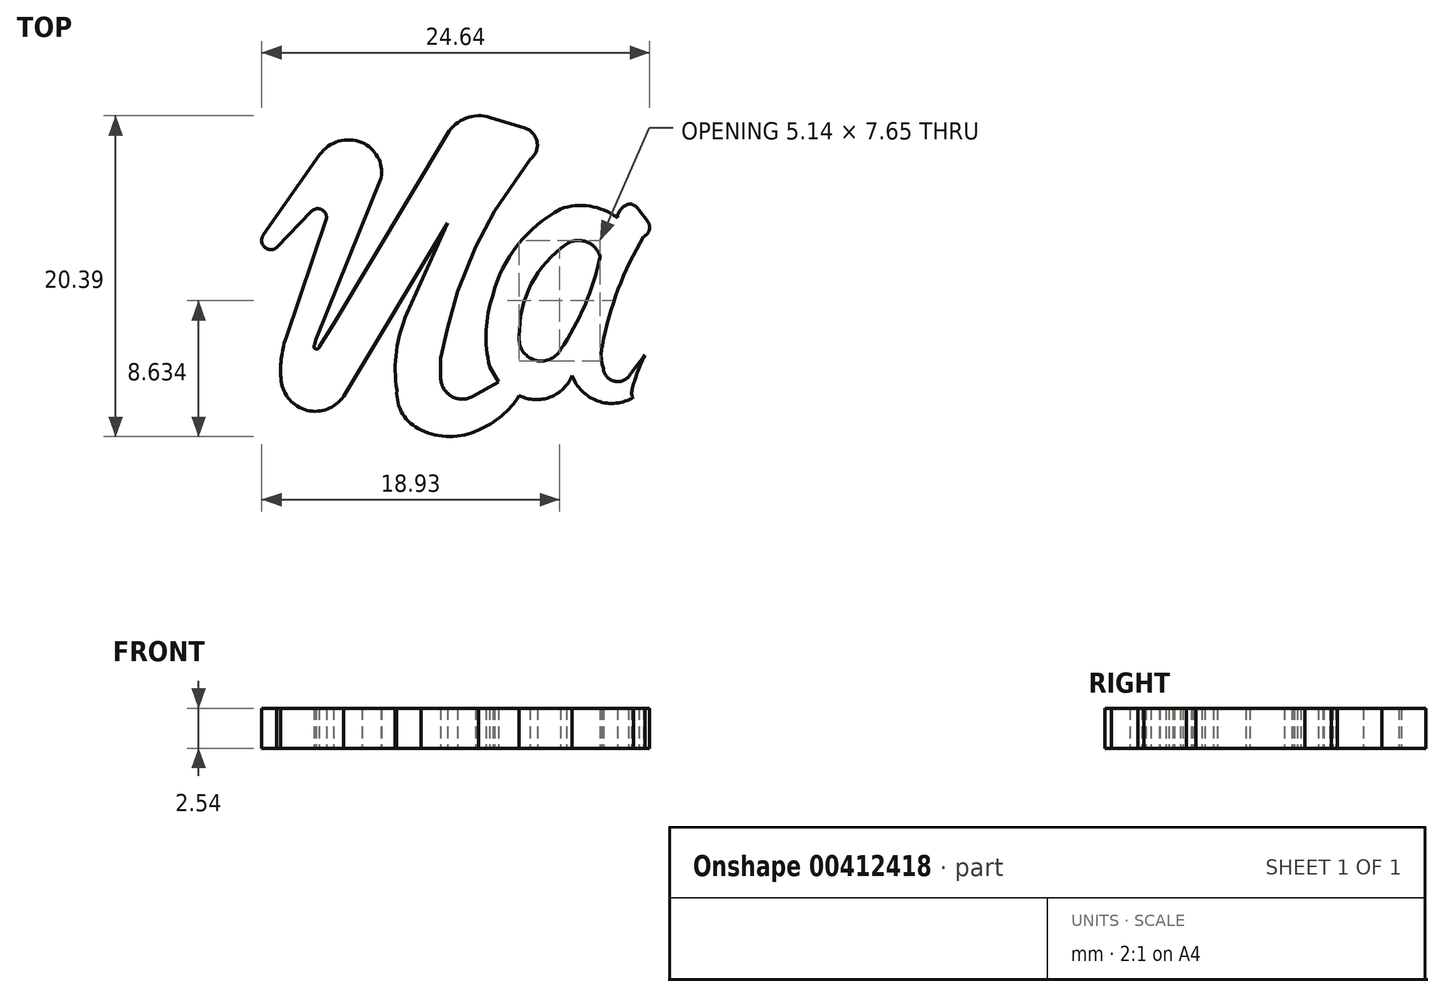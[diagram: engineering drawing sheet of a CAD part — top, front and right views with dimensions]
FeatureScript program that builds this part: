
annotation { "Feature Type Name" : "Feature", "Feature Type Description" : "" }
export const myFeature = defineFeature(function(context is Context, id is Id, definition is map)
    precondition{}
    {
        {
            var Q0;
            Q0=qCreatedBy(makeId("Top.planeOp"),FACE);
            var sketch = newSketch(context, id + "F0", { "sketchPlane" : qUnion([Q0])});
            skArc(sketch, "E0", {"start": v(0.44, -13.61) * mm, "mid": v(0.52, -14.38) * mm, "end": v(1.29, -14.39) * mm});
            skLineSegment(sketch, "E1", {"start": v(0.44, -13.61) * mm, "end": v(4.02, -8.5) * mm});
            skLineSegment(sketch, "E2", {"start": v(1.29, -14.39) * mm, "end": v(3.51, -12.1) * mm});
            skArc(sketch, "E3", {"start": v(6.7, -7.72) * mm, "mid": v(5.22, -7.65) * mm, "end": v(4.02, -8.5) * mm});
            skArc(sketch, "E4", {"start": v(7.92, -9.98) * mm, "mid": v(7.7, -8.64) * mm, "end": v(6.7, -7.72) * mm});
            skLineSegment(sketch, "E5", {"start": v(7.92, -9.98) * mm, "end": v(3.78, -20.22) * mm});
            skLineSegment(sketch, "E6", {"start": v(3.78, -20.22) * mm, "end": v(3.68, -20.57) * mm});
            skLineSegment(sketch, "E7", {"start": v(3.98, -20.73) * mm, "end": v(4.9, -19.24) * mm});
            skArc(sketch, "E8", {"start": v(3.68, -20.57) * mm, "mid": v(3.74, -20.83) * mm, "end": v(3.98, -20.73) * mm});
            skLineSegment(sketch, "E9", {"start": v(4.9, -19.24) * mm, "end": v(12.13, -7.17) * mm});
            skArc(sketch, "E10", {"start": v(14.84, -6.13) * mm, "mid": v(13.3, -6.18) * mm, "end": v(12.13, -7.17) * mm});
            skLineSegment(sketch, "E11", {"start": v(14.84, -6.13) * mm, "end": v(17.05, -6.8) * mm});
            skArc(sketch, "E12", {"start": v(17.36, -8.8) * mm, "mid": v(17.83, -7.7) * mm, "end": v(17.05, -6.8) * mm});
            skLineSegment(sketch, "E13", {"start": v(17.36, -8.8) * mm, "end": v(15.1, -12.1) * mm});
            skLineSegment(sketch, "E14", {"start": v(15.1, -12.1) * mm, "end": v(13.92, -14.37) * mm});
            skLineSegment(sketch, "E15", {"start": v(13.92, -14.37) * mm, "end": v(12.79, -17.18) * mm});
            skLineSegment(sketch, "E16", {"start": v(12.79, -17.18) * mm, "end": v(12.15, -19.5) * mm});
            skLineSegment(sketch, "E17", {"start": v(12.15, -19.5) * mm, "end": v(11.7, -21.43) * mm});
            skLineSegment(sketch, "E18", {"start": v(11.7, -21.43) * mm, "end": v(11.7, -22.67) * mm});
            skArc(sketch, "E19", {"start": v(11.7, -22.67) * mm, "mid": v(12.37, -23.84) * mm, "end": v(13.73, -23.85) * mm});
            skLineSegment(sketch, "E20", {"start": v(13.73, -23.85) * mm, "end": v(15.36, -22.93) * mm});
            skLineSegment(sketch, "E21", {"start": v(15.36, -22.93) * mm, "end": v(14.82, -21.97) * mm});
            skArc(sketch, "E22", {"start": v(15.01, -17.43) * mm, "mid": v(14.59, -19.68) * mm, "end": v(14.82, -21.97) * mm});
            skArc(sketch, "E23", {"start": v(19.3, -11.94) * mm, "mid": v(16.6, -14.24) * mm, "end": v(15.01, -17.43) * mm});
            skArc(sketch, "E24", {"start": v(22.92, -12.49) * mm, "mid": v(21.18, -11.77) * mm, "end": v(19.3, -11.94) * mm});
            skArc(sketch, "E25", {"start": v(21.83, -15) * mm, "mid": v(20.98, -14.04) * mm, "end": v(19.7, -14.17) * mm});
            skArc(sketch, "E26", {"start": v(16.7, -20.05) * mm, "mid": v(17.66, -21.54) * mm, "end": v(19.3, -20.89) * mm});
            skArc(sketch, "E27", {"start": v(19.7, -14.17) * mm, "mid": v(17.45, -16.73) * mm, "end": v(16.7, -20.05) * mm});
            skArc(sketch, "E28", {"start": v(19.3, -20.89) * mm, "mid": v(20.86, -18.07) * mm, "end": v(21.83, -15) * mm});
            skArc(sketch, "E29", {"start": v(16.7, -23.8) * mm, "mid": v(18.65, -23.9) * mm, "end": v(20.05, -22.52) * mm});
            skArc(sketch, "E30", {"start": v(22.03, -22.07) * mm, "mid": v(22.82, -22.9) * mm, "end": v(23.8, -22.32) * mm});
            skArc(sketch, "E31", {"start": v(20.05, -22.52) * mm, "mid": v(21.67, -24.14) * mm, "end": v(23.95, -23.9) * mm});
            skArc(sketch, "E32", {"start": v(1.57, -22.86) * mm, "mid": v(3.2, -24.73) * mm, "end": v(5.52, -23.85) * mm});
            skArc(sketch, "E33", {"start": v(4.44, -12.54) * mm, "mid": v(4.13, -11.98) * mm, "end": v(3.51, -12.1) * mm});
            skLineSegment(sketch, "E34", {"start": v(4.44, -12.54) * mm, "end": v(1.87, -20.15) * mm});
            skArc(sketch, "E35", {"start": v(1.87, -20.15) * mm, "mid": v(1.57, -21.49) * mm, "end": v(1.57, -22.86) * mm});
            skLineSegment(sketch, "E36", {"start": v(5.52, -23.85) * mm, "end": v(12.15, -12.83) * mm});
            skLineSegment(sketch, "E37", {"start": v(12.15, -12.83) * mm, "end": v(9.58, -18.57) * mm});
            skArc(sketch, "E38", {"start": v(9.58, -18.57) * mm, "mid": v(8.9, -20.97) * mm, "end": v(8.92, -23.46) * mm});
            skArc(sketch, "E39", {"start": v(8.92, -23.46) * mm, "mid": v(9.29, -24.97) * mm, "end": v(10.45, -25.98) * mm});
            skArc(sketch, "E40", {"start": v(10.45, -25.98) * mm, "mid": v(12.28, -26.4) * mm, "end": v(14.1, -25.98) * mm});
            skArc(sketch, "E41", {"start": v(14.1, -25.98) * mm, "mid": v(15.57, -25.1) * mm, "end": v(16.7, -23.8) * mm});
            skArc(sketch, "E42", {"start": v(23.64, -11.63) * mm, "mid": v(23.16, -11.95) * mm, "end": v(22.92, -12.49) * mm});
            skArc(sketch, "E43", {"start": v(24.29, -12.02) * mm, "mid": v(24.02, -11.73) * mm, "end": v(23.64, -11.63) * mm});
            skLineSegment(sketch, "E44", {"start": v(24.29, -12.02) * mm, "end": v(24.83, -12.71) * mm});
            skArc(sketch, "E45", {"start": v(24.58, -13.7) * mm, "mid": v(24.95, -13.27) * mm, "end": v(24.83, -12.71) * mm});
            skArc(sketch, "E46", {"start": v(24.58, -13.7) * mm, "mid": v(22.97, -17.05) * mm, "end": v(21.96, -20.62) * mm});
            skArc(sketch, "E47", {"start": v(21.96, -20.62) * mm, "mid": v(21.9, -21.35) * mm, "end": v(22.03, -22.07) * mm});
            skFitSpline(sketch, "E48", {"points": [v(24.66, -21.23) * mm, v(26.09, -18.34) * mm, v(26.73, -14.68) * mm, v(26.2, -10.48) * mm, v(25.33, -8.21) * mm, v(25.34, -7.66) * mm, v(25.92, -7.22) * mm, v(27.77, -6.23) * mm, v(28.48, -6.17) * mm, v(28.83, -6.67) * mm, v(29.15, -9.2) * mm, v(29.21, -11.8) * mm, v(29.15, -14.25) * mm, v(29.13, -15.57) * mm, v(29.38, -15.18) * mm, v(29.75, -13.94) * mm, v(31.5, -7) * mm, v(31.92, -5.4) * mm, v(32.5, -4.97) * mm, v(33.79, -4.6) * mm, v(36.42, -4.48) * mm, v(36.99, -4.63) * mm, v(37.3, -5.31) * mm, v(37.06, -6.27) * mm, v(34.06, -14.63) * mm, v(33.67, -15.91) * mm, v(33.91, -15.61) * mm, v(35.35, -12.6) * mm, v(37.8, -7.41) * mm, v(38.27, -6.47) * mm, v(38.71, -5.86) * mm, v(39.24, -5.62) * mm, v(40.15, -5.89) * mm, v(41.89, -7.18) * mm, v(42.06, -7.68) * mm, v(41.74, -8.68) * mm, v(40.21, -11.59) * mm, v(39.27, -14.16) * mm, v(38.3, -17.42) * mm, v(38.44, -19.03) * mm, v(38.82, -20.12) * mm, v(39.65, -20.71) * mm, v(39.7, -20.21) * mm, v(39.76, -18.01) * mm, v(41.06, -14.98) * mm, v(42.18, -13.3) * mm, v(43.17, -12.26) * mm, v(44.34, -11.64) * mm, v(45.3, -11.45) * mm, v(46.51, -11.49) * mm, v(47.7, -11.9) * mm, v(47.96, -12.1) * mm, v(48.46, -11.3) * mm, v(48.95, -11.15) * mm, v(50.1, -12.6) * mm, v(49.94, -13.05) * mm, v(48.65, -15.34) * mm, v(47.36, -18.98) * mm, v(47.1, -20.7) * mm, v(47.16, -21.54) * mm, v(47.61, -22.32) * mm, v(48.25, -22.7) * mm, v(50.37, -19.94) * mm, v(50.56, -17.82) * mm, v(50.69, -15) * mm, v(51.26, -13.7) * mm, v(52.16, -12.95) * mm, v(53.14, -12.71) * mm, v(54.42, -13.26) * mm, v(55.21, -15.18) * mm, v(55.07, -16.22) * mm, v(54.47, -16.81) * mm, v(53.49, -16.66) * mm, v(53.09, -16.12) * mm, v(52.9, -16.42) * mm, v(52.45, -18) * mm, v(52.65, -20.57) * mm, v(53.53, -21.75) * mm, v(54.72, -21.8) * mm, v(56.25, -20.32) * mm, v(57.2, -17.26) * mm, v(56.94, -14.5) * mm, v(55.76, -11.97) * mm, v(53.88, -11.28) * mm, v(53.14, -11.38) * mm, v(52.3, -10.64) * mm, v(52.9, -8.86) * mm, v(53.87, -5.9) * mm, v(55.02, -4.17) * mm, v(56.7, -3.91) * mm, v(57.9, -4.68) * mm, v(57.72, -6.1) * mm, v(57.14, -7.12) * mm, v(56.88, -7.12) * mm, v(56.5, -6.48) * mm, v(55.73, -6.35) * mm, v(55.02, -7.12) * mm, v(54.77, -7.89) * mm, v(55.47, -8.66) * mm, v(57.08, -9.17) * mm, v(58.61, -10.64) * mm, v(59.38, -13.14) * mm, v(59.64, -12.18) * mm, v(60.34, -9.75) * mm, v(60.92, -8.14) * mm, v(61.05, -7.31) * mm, v(60.28, -6.54) * mm, v(59.38, -5.58) * mm, v(59.64, -4.17) * mm, v(60.66, -3.15) * mm, v(61.75, -3.34) * mm, v(62.14, -3.91) * mm, v(62.9, -0.9) * mm, v(63.7, 2.4) * mm, v(64.34, 3.2) * mm, v(65.77, 3.4) * mm, v(67.06, 2.26) * mm, v(67.06, 0.43) * mm, v(66.47, -0.9) * mm, v(65.23, -3.23) * mm, v(64.4, -4.83) * mm, v(64.28, -5.54) * mm, v(64.66, -6.11) * mm, v(65.43, -6.88) * mm, v(65.5, -7.84) * mm, v(64.73, -8.61) * mm, v(64.22, -8.74) * mm, v(63.51, -8.3) * mm, v(62.87, -8.55) * mm, v(61.46, -13.35) * mm, v(61.46, -17.84) * mm, v(62.1, -19.44) * mm, v(63, -19.57) * mm, v(64.22, -18.35) * mm, v(64.73, -17.13) * mm, v(64.98, -14.06) * mm, v(65.75, -10.86) * mm, v(67.3, -8.93) * mm, v(69.15, -8.42) * mm, v(71.33, -8.93) * mm, v(72.03, -10.34) * mm, v(71.07, -12.84) * mm, v(69.53, -14.96) * mm, v(66.71, -17.71) * mm, v(67.16, -18.29) * mm, v(67.93, -19.06) * mm, v(69.28, -19.38) * mm, v(70.62, -18.86) * mm, v(72.74, -16.5) * mm, v(73.7, -14.83) * mm, v(74.27, -14.44) * mm, v(74.72, -14.7) * mm, v(74.72, -15.15) * mm, v(73, -19.44) * mm, v(71.52, -21.23) * mm, v(69.53, -21.88) * mm, v(67.23, -21.23) * mm, v(65.56, -19.63) * mm, v(65.43, -19.7) * mm, v(64.66, -21.23) * mm, v(63, -23.29) * mm, v(61.59, -23.9) * mm, v(59.99, -23.41) * mm, v(59.35, -21.56) * mm, v(59.09, -19.38) * mm, v(58.96, -18.35) * mm, v(58.83, -18.48) * mm, v(58.26, -20.34) * mm, v(56.46, -22.97) * mm, v(54.13, -24.2) * mm, v(52.05, -23.45) * mm, v(51.06, -21.95) * mm, v(50.4, -22.7) * mm, v(48.4, -23.9) * mm, v(46.4, -23.45) * mm, v(45.24, -22.32) * mm, v(45.1, -22.32) * mm, v(43.9, -23.62) * mm, v(42.28, -23.9) * mm, v(40.84, -22.97) * mm, v(40.74, -23.02) * mm, v(39.56, -23.9) * mm, v(38.22, -24.26) * mm, v(36.64, -23.9) * mm, v(35.85, -23.12) * mm, v(35.8, -20.8) * mm, v(36.4, -17.3) * mm, v(38.73, -10.45) * mm, v(38.73, -10.3) * mm, v(38.38, -10.9) * mm, v(34.28, -19.4) * mm, v(32.2, -23.4) * mm, v(31.12, -24.62) * mm, v(30.18, -24.36) * mm, v(29.89, -23.08) * mm, v(30.38, -20.8) * mm, v(31.91, -15.27) * mm, v(32.58, -12) * mm, v(32.63, -10.98) * mm, v(32.48, -10.98) * mm, v(31.05, -14.69) * mm, v(29.33, -19.19) * mm, v(27.85, -22.8) * mm, v(27.16, -23.63) * mm, v(26.27, -23.53) * mm, v(26.02, -22.32) * mm, v(25.87, -22.32) * mm, v(23.95, -23.9) * mm, v(24.66, -21.23) * mm]});
            skLineSegment(sketch, "E49", {"start": v(23.8, -22.32) * mm, "end": v(24.66, -21.23) * mm});
            skFitSpline(sketch, "E50", {"points": [v(66.38, -15.8) * mm, v(67.93, -14.1) * mm, v(69.26, -12.4) * mm, v(69.58, -11.55) * mm, v(69.34, -11.08) * mm, v(68.43, -11.2) * mm, v(66.7, -12.96) * mm, v(66.26, -14.84) * mm, v(66.23, -15.46) * mm, v(66.38, -15.8) * mm]});
            skFitSpline(sketch, "E51", {"points": [v(44.56, -20.2) * mm, v(45.7, -18) * mm, v(46.85, -15.18) * mm, v(46.96, -14.42) * mm, v(46.24, -13.54) * mm, v(44.56, -13.7) * mm, v(43.11, -15.33) * mm, v(42, -17.7) * mm, v(41.82, -19.33) * mm, v(42.16, -20.67) * mm, v(42.77, -21.24) * mm, v(43.68, -21.09) * mm, v(44.56, -20.2) * mm]});
            skSolve(sketch);
        }
        {
            var Q0;
            Q0=makeQuery(id+"F0.imprint","IMPRINT",FACE,{"disambiguationData":[TD([[makeQuery(id+"F0.imprint","IMPRINT",EDGE,{"derivedFrom":sQuery(id+"F0.wireOp",EDGE,"E0")}),1.0]])]});
            extrude(context, id + "F1", {"entities" : qUnion([Q0]), "depth" : 2.54 * mm});
        }
    });
